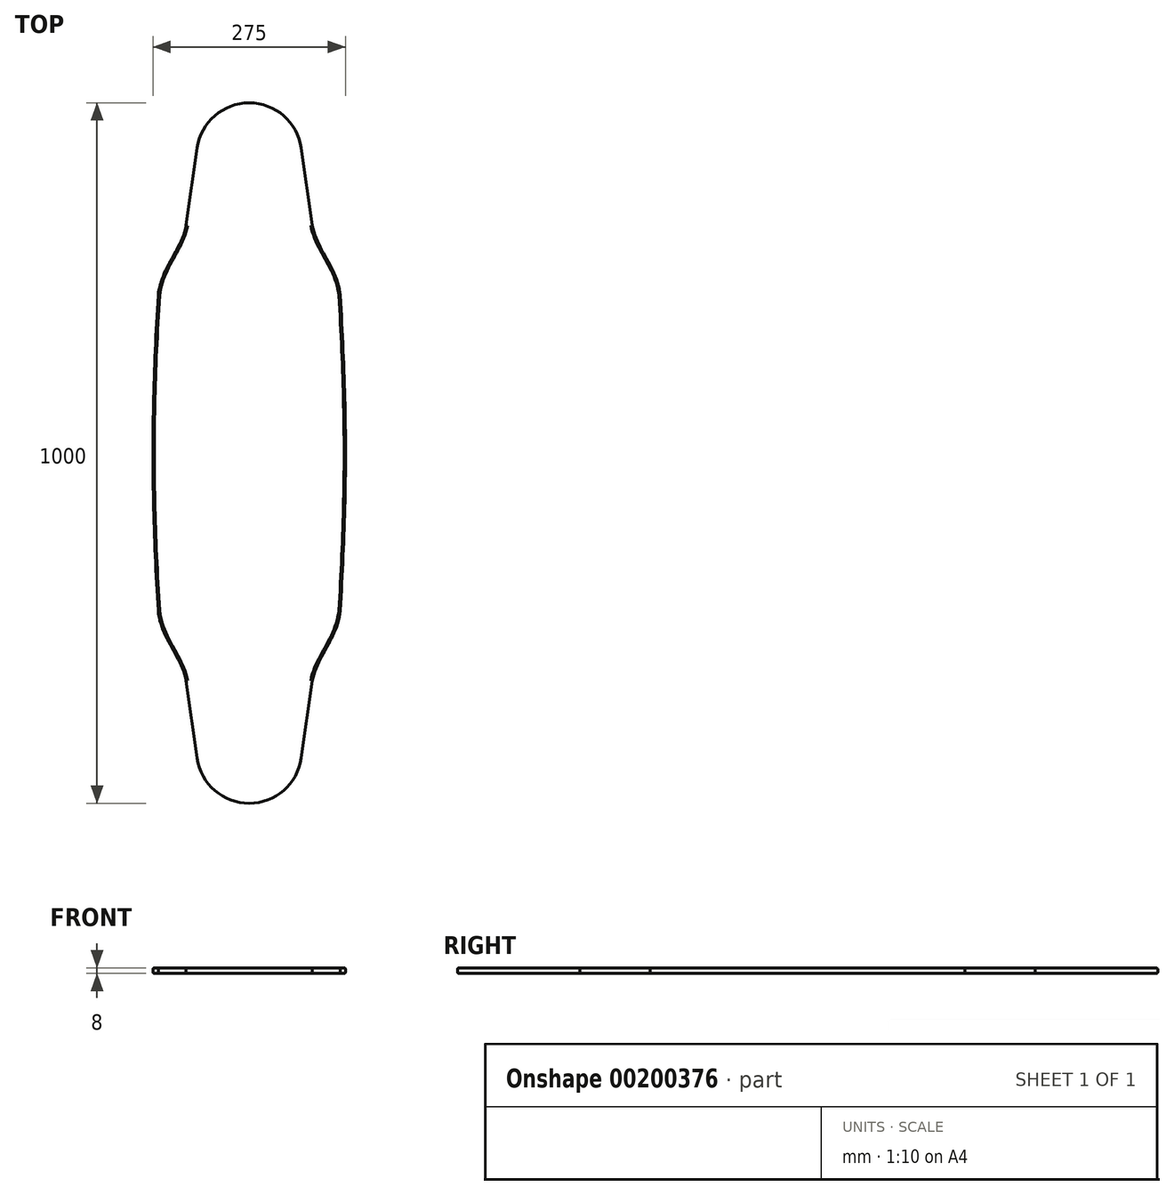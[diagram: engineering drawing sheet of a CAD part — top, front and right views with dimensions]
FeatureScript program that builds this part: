
annotation { "Feature Type Name" : "Feature", "Feature Type Description" : "" }
export const myFeature = defineFeature(function(context is Context, id is Id, definition is map)
    precondition{}
    {
        {
            var Q0;
            Q0=qCreatedBy(makeId("Top.planeOp"),FACE);
            var sketch = newSketch(context, id + "F0", { "sketchPlane" : qUnion([Q0])});
            skLineSegment(sketch, "E0", {"start": v(0, 0) * mm, "end": v(0, 500) * mm});
            skLineSegment(sketch, "E1", {"start": v(0, 0) * mm, "end": v(0, -500) * mm});
            skLineSegment(sketch, "E2", {"start": v(0, 0) * mm, "end": v(-200, 0) * mm});
            skLineSegment(sketch, "E3", {"start": v(0, 0) * mm, "end": v(200, 0) * mm});
            skPoint(sketch, "E4", {"position": v(-130, -225) * mm});
            skPoint(sketch, "E5", {"position": v(-130, 225) * mm});
            skFitSpline(sketch, "E6", {"points": [v(-130, -225) * mm, v(-130, 225) * mm], "startDerivative": vector(-30, 491.67) * mm, "endDerivative": vector(30, 491.67) * mm});
            skCircle(sketch, "E7", {"center": v(0, 425) * mm, "radius": 75 * mm});
            skPoint(sketch, "E8", {"position": v(-90, 325) * mm});
            skLineSegment(sketch, "E9", {"start": v(-90, 325) * mm, "end": v(-74.25, 435.58) * mm});
            skLineSegment(sketch, "E10.MirrorCS", {"start": v(-90, -325) * mm, "end": v(-74.25, -435.58) * mm});
            skCircle(sketch, "E11.MirrorC", {"center": v(0, -425) * mm, "radius": 75 * mm});
            skLineSegment(sketch, "E12.MirrorCS", {"start": v(90, 325) * mm, "end": v(74.25, 435.58) * mm});
            skFitSpline(sketch, "E13.MirrorCS", {"points": [v(130, -225) * mm, v(130, 225) * mm], "startDerivative": vector(30, 491.67) * mm, "endDerivative": vector(-30, 491.67) * mm});
            skLineSegment(sketch, "E14.MirrorCS", {"start": v(90, -325) * mm, "end": v(74.25, -435.58) * mm});
            skFitSpline(sketch, "E15", {"points": [v(130, -225) * mm, v(90, -325) * mm], "startDerivative": vector(-12.1, -118.87) * mm, "endDerivative": vector(-19.61, -104.4) * mm});
            skFitSpline(sketch, "E16.MirrorCS", {"points": [v(-130, -225) * mm, v(-90, -325) * mm], "startDerivative": vector(12.1, -118.87) * mm, "endDerivative": vector(19.61, -104.4) * mm});
            skFitSpline(sketch, "E17.MirrorCS", {"points": [v(-130, 225) * mm, v(-90, 325) * mm], "startDerivative": vector(12.1, 118.87) * mm, "endDerivative": vector(19.61, 104.4) * mm});
            skFitSpline(sketch, "E18.MirrorCS", {"points": [v(130, 225) * mm, v(90, 325) * mm], "startDerivative": vector(-12.1, 118.87) * mm, "endDerivative": vector(-19.61, 104.4) * mm});
            skSolve(sketch);
        }
        {
            var Q0;
            Q0 = qSketchRegion(id + "F0", true);
            extrude(context, id + "F1", {"entities" : qUnion([Q0]), "depth" : 8 * mm});
        }
        {
            var Q0;
            Q0=makeQuery(id+"F1.opExtrude","CAP_FACE",FACE,{"disambiguationData":[OSD([sQuery(id+"F0.wireOp",EDGE,"E6"),sQuery(id+"F0.wireOp",EDGE,"E9"),sQuery(id+"F0.wireOp",EDGE,"E10.MirrorCS"),sQuery(id+"F0.wireOp",EDGE,"E7"),sQuery(id+"F0.wireOp",EDGE,"E12.MirrorCS"),sQuery(id+"F0.wireOp",EDGE,"E13.MirrorCS"),sQuery(id+"F0.wireOp",EDGE,"E11.MirrorC"),sQuery(id+"F0.wireOp",EDGE,"E14.MirrorCS"),sQuery(id+"F0.wireOp",EDGE,"E15"),sQuery(id+"F0.wireOp",EDGE,"E16.MirrorCS"),sQuery(id+"F0.wireOp",EDGE,"E17.MirrorCS"),sQuery(id+"F0.wireOp",EDGE,"E18.MirrorCS")])],"isStart":false});
            var Q1;
            Q1=makeQuery(id+"F1.opExtrude","CAP_FACE",FACE,{"disambiguationData":[OSD([sQuery(id+"F0.wireOp",EDGE,"E6"),sQuery(id+"F0.wireOp",EDGE,"E9"),sQuery(id+"F0.wireOp",EDGE,"E10.MirrorCS"),sQuery(id+"F0.wireOp",EDGE,"E7"),sQuery(id+"F0.wireOp",EDGE,"E12.MirrorCS"),sQuery(id+"F0.wireOp",EDGE,"E13.MirrorCS"),sQuery(id+"F0.wireOp",EDGE,"E11.MirrorC"),sQuery(id+"F0.wireOp",EDGE,"E14.MirrorCS"),sQuery(id+"F0.wireOp",EDGE,"E15"),sQuery(id+"F0.wireOp",EDGE,"E16.MirrorCS"),sQuery(id+"F0.wireOp",EDGE,"E17.MirrorCS"),sQuery(id+"F0.wireOp",EDGE,"E18.MirrorCS")])],"isStart":true});
            fillet(context, id + "F2", {"entities" : qUnion([Q0, Q1]), "radius" : 2 * mm, "tangentPropagation" : true, "allowEdgeOverflow" : false});
        }
    });
